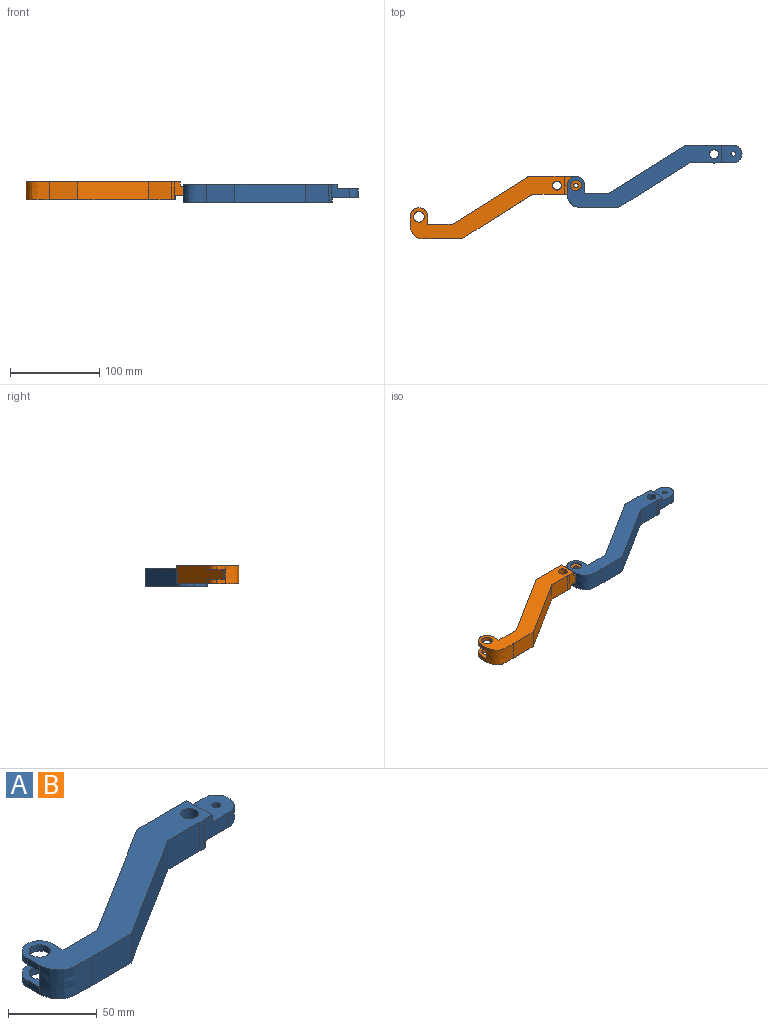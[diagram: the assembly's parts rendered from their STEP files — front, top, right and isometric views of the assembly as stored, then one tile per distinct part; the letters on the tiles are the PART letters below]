
ASSEMBLY  parts=2 mates=1
PART A: 41 faces, bbox 196.2x70.5x20 mm
  f0: cylinder r=10mm len=10mm, axis (0,0,-1), area 1.7mm2, adj f7,f36,f39
  f1: plane 20x19.56mm, normal (0,-1,0), area 229.6mm2, adj f2,f8,f17,f31,f36,f37,f39,f40
  f2: cylinder r=10mm len=10mm, axis (0,0,-1), area 144.9mm2, adj f1,f3,f36,f39
  f3: plane 10x0.06mm, normal (0.99,-0.12,0), area 0.6mm2, adj f2,f4,f36,f39
  f4: cylinder r=10mm len=11.21mm, axis (0,0,-1), area 169.3mm2, adj f3,f5,f36,f39
  f5: plane 51.74x20mm, normal (0,1,0), area 873.3mm2, adj f4,f8,f18,f31,f36,f38,f39,f40
  f6: cylinder r=2.5mm len=10mm, axis (0,0,-1), area 157.1mm2, adj f36,f39
  f7: plane 10x0.17mm, normal (1,0,0), area 1.7mm2, adj f0,f36,f39
  f8: plane 172.74x70.45mm, normal (0,0,1), area 3583.4mm2, adj f1,f5,f9,f10,f11,f17,f18,f19
  f9: cylinder r=5mm len=20mm, axis (0,0,-1), area 575.2mm2, adj f8,f31,f36,f37,f38
  f10: plane 9.69x4.3mm, normal (-1,0,0), area 41.7mm2, adj f8,f24,f26,f34
  f11: plane 25.96x20mm, normal (0,1,0), area 410.7mm2, adj f8,f12,f20,f21,f31,f32,f34,f35
  f12: plane 8.6x4.81mm, normal (1,0,0), area 41.3mm2, adj f11,f13,f31,f32
  f13: cylinder r=10mm len=10mm, axis (0,0,-1), area 75.5mm2, adj f12,f14,f31,f32
  f14: plane 4.81x0.03mm, normal (0,1,0), area 0.2mm2, adj f13,f15,f31,f32
  f15: cylinder r=10mm len=10mm, axis (0,0,-1), area 75.5mm2, adj f14,f25,f31,f32
  f16: cylinder r=6mm len=12mm, axis (0,0,-1), area 181.3mm2, adj f31,f32
  f17: cylinder r=10mm len=20mm, axis (0,0,-1), area 71.8mm2, adj f1,f8,f30,f31
  f18: cylinder r=5mm len=20mm, axis (0,0,-1), area 56mm2, adj f5,f8,f19,f31
  f19: plane 83.09x52.27mm, normal (-0.53,0.85,0), area 1963.2mm2, adj f8,f18,f20,f31
  f20: cylinder r=5mm len=20mm, axis (0,0,-1), area 56.2mm2, adj f8,f11,f19,f31
  f21: plane 8.6x4.3mm, normal (1,0,0), area 37mm2, adj f8,f11,f22,f34
  f22: cylinder r=10mm len=10mm, axis (0,0,-1), area 67.6mm2, adj f8,f21,f23,f34
  f23: plane 4.3x0.03mm, normal (0,1,0), area 0.1mm2, adj f8,f22,f24,f34
  f24: cylinder r=10mm len=10mm, axis (0,0,-1), area 67.6mm2, adj f8,f10,f23,f34
  f25: plane 9.69x4.81mm, normal (-1,0,0), area 46.6mm2, adj f15,f26,f31,f32
  f26: extruded ~26.43x20mm, area 703.8mm2, adj f8,f10,f25,f27,f31,f33
  f27: plane 31.65x20mm, normal (0,-1,0), area 633mm2, adj f8,f26,f28,f31
  f28: plane 79.48x50mm, normal (0.53,-0.85,0), area 1878mm2, adj f8,f27,f30,f31
  f29: cylinder r=6mm len=12mm, axis (0,0,-1), area 162.2mm2, adj f8,f34
  f30: plane 25.45x20mm, normal (0,-1,0), area 509.1mm2, adj f8,f17,f28,f31
  f31: plane 167.24x70.45mm, normal (0,0,-1), area 3489mm2, adj f1,f5,f9,f11,f12,f13,f14,f15
  f32: plane 30x19.69mm, normal (0,0,1), area 249.3mm2, adj f11,f12,f13,f14,f15,f16,f25,f33
  f33: plane 30x10.89mm, normal (0,1,0), area 326.6mm2, adj f26,f32,f34,f35
  f34: plane 30x19.69mm, normal (0,0,-1), area 249.3mm2, adj f10,f11,f21,f22,f23,f24,f29,f33
  f35: plane 10.89x1.09mm, normal (-1,0,0), area 11.9mm2, adj f11,f32,f33,f34
  f36: plane 28.92x20.06mm, normal (0,0,-1), area 501.3mm2, adj f0,f1,f2,f3,f4,f5,f6,f7
  f37: plane 5.47x5mm, normal (1,0,0), area 27.4mm2, adj f1,f9,f31,f36
  f38: plane 5.83x5mm, normal (1,0,0), area 29.2mm2, adj f5,f9,f31,f36
  f39: plane 23.41x20.06mm, normal (0,0,1), area 406.9mm2, adj f0,f1,f2,f3,f4,f5,f6,f7
  f40: plane 20.04x5mm, normal (1,0,0), area 100.2mm2, adj f1,f5,f8,f39
PART B: same geometry as A
PLACE A t=(-165.64,-44.95,5)mm
PLACE B t=(-341.76,-80.21,7.85)mm
MATE revolute A.f13 <-> B.f4  axis (0,0,-1) through (-176.12,-35.26,12.85)mm
